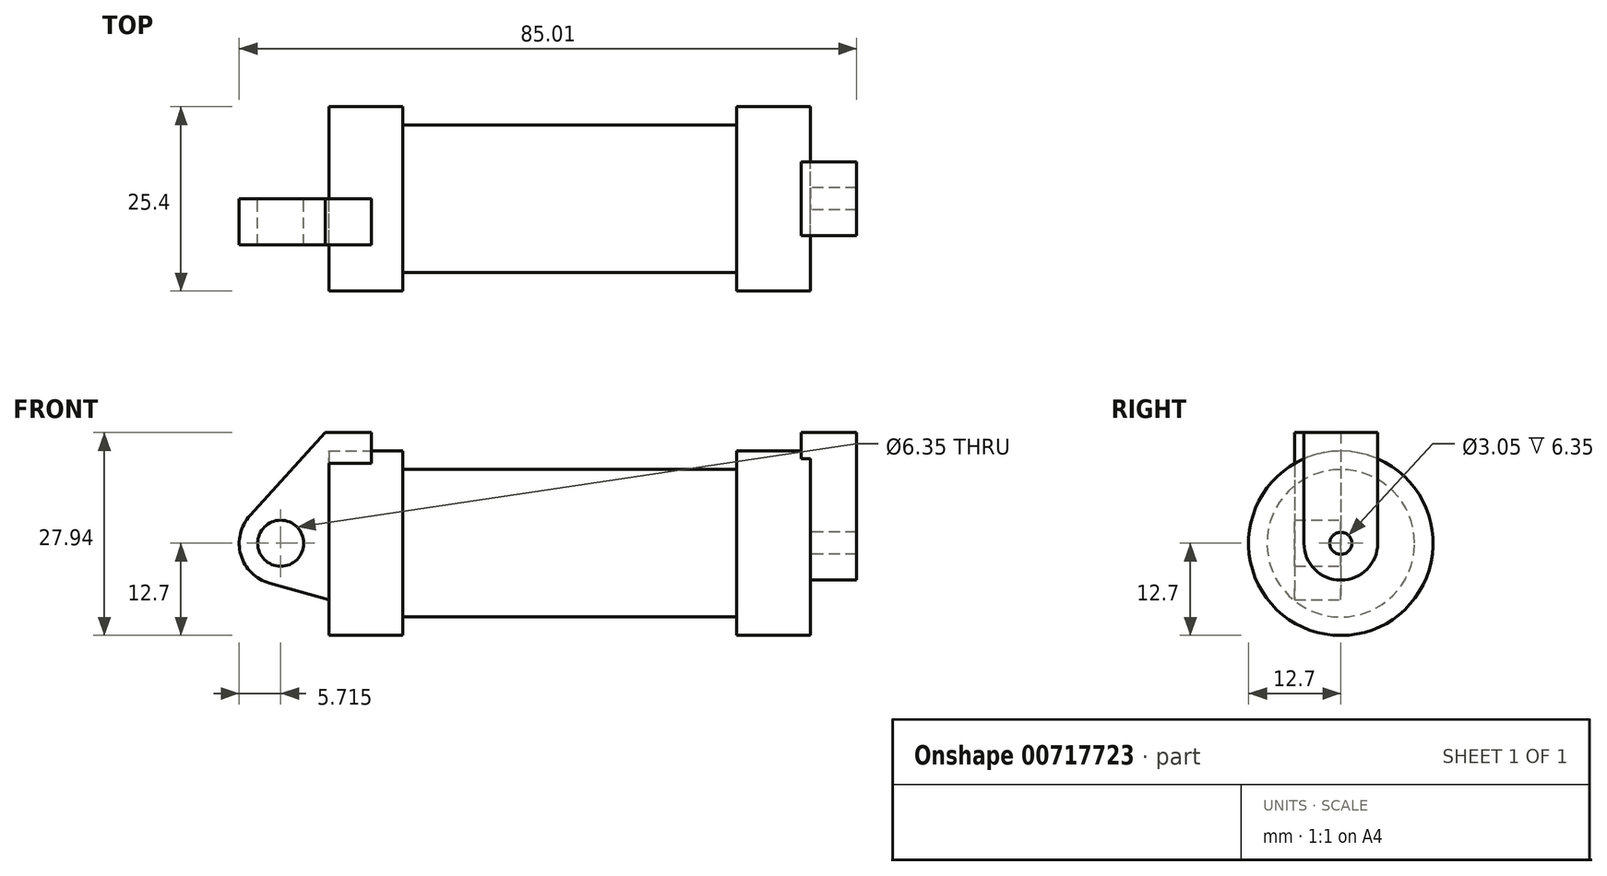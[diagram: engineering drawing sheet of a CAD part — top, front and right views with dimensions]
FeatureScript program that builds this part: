
annotation { "Feature Type Name" : "Feature", "Feature Type Description" : "" }
export const myFeature = defineFeature(function(context is Context, id is Id, definition is map)
    precondition{}
    {
        {
            var Q0;
            Q0=qCreatedBy(makeId("Front.planeOp"),FACE);
            var sketch = newSketch(context, id + "F0", { "sketchPlane" : qUnion([Q0])});
            skLineSegment(sketch, "E0", {"start": v(0, 0) * mm, "end": v(0, 12.7) * mm});
            skLineSegment(sketch, "E1", {"start": v(0, 12.7) * mm, "end": v(10.16, 12.7) * mm});
            skLineSegment(sketch, "E2", {"start": v(10.16, 12.7) * mm, "end": v(10.16, 10.16) * mm});
            skLineSegment(sketch, "E3", {"start": v(10.16, 10.16) * mm, "end": v(56.13, 10.16) * mm});
            skLineSegment(sketch, "E4", {"start": v(56.13, 10.16) * mm, "end": v(56.13, 12.7) * mm});
            skLineSegment(sketch, "E5", {"start": v(56.13, 12.7) * mm, "end": v(66.3, 12.7) * mm});
            skLineSegment(sketch, "E6", {"start": v(66.3, 12.7) * mm, "end": v(66.3, 0) * mm});
            skLineSegment(sketch, "E7", {"start": v(66.3, 0) * mm, "end": v(0, 0) * mm});
            skLineSegment(sketch, "E8", {"start": v(5.84, 15.24) * mm, "end": v(-0.5, 15.24) * mm});
            skLineSegment(sketch, "E9", {"start": v(-0.5, 15.24) * mm, "end": v(-10.88, 3.85) * mm});
            skLineSegment(sketch, "E10", {"start": v(0, 0) * mm, "end": v(-6.65, 0) * mm});
            skCircle(sketch, "E11", {"center": v(-6.65, 0) * mm, "radius": 5.72 * mm});
            skCircle(sketch, "E12", {"center": v(-6.65, 0) * mm, "radius": 3.18 * mm});
            skLineSegment(sketch, "E13", {"start": v(5.84, 15.24) * mm, "end": v(5.84, -9.4) * mm});
            skLineSegment(sketch, "E14", {"start": v(5.84, -9.4) * mm, "end": v(-8.18, -5.5) * mm});
            skSolve(sketch);
        }
        {
            var Q0;
            {var subQ0=sQuery(id+"F0.wireOp",EDGE,"E2");Q0=makeQuery(id+"F0.imprint","IMPRINT",FACE,{"disambiguationData":[TD([[makeQuery(id+"F0.imprint","IMPRINT",EDGE,{"derivedFrom":subQ0}),-1.0]])]});}
            var Q1;
            {var subQ0=sQuery(id+"F0.wireOp",EDGE,"E0");Q1=makeQuery(id+"F0.imprint","IMPRINT",FACE,{"disambiguationData":[TD([[makeQuery(id+"F0.imprint","IMPRINT",EDGE,{"derivedFrom":subQ0}),-1.0]])]});}
            var Q2;
            Q2=sQuery(id+"F0.wireOp",EDGE,"E7");
            revolve(context, id + "F1", {"surfaceOperationType" : NewSurfaceOperationType.NEW, "entities" : qUnion([Q0, Q1]), "axis" : qUnion([Q2]), "revolveType" : RevolveType.FULL});
        }
        {
            var Q0;
            {var subQ1=sQuery(id+"F0.wireOp",EDGE,"E0");Q0=makeQuery(id+"F0.imprint","IMPRINT",FACE,{"disambiguationData":[TD([[makeQuery(id+"F0.imprint","IMPRINT",EDGE,{"derivedFrom":subQ1}),1.0]])]});}
            var Q1;
            {var subQ0=sQuery(id+"F0.wireOp",EDGE,"E14");Q1=makeQuery(id+"F0.imprint","IMPRINT",FACE,{"disambiguationData":[TD([[makeQuery(id+"F0.imprint","IMPRINT",EDGE,{"derivedFrom":subQ0}),-1.0]])]});}
            var Q2;
            {var subQ0=sQuery(id+"F0.wireOp",EDGE,"E0");Q2=makeQuery(id+"F0.imprint","IMPRINT",FACE,{"disambiguationData":[TD([[makeQuery(id+"F0.imprint","IMPRINT",EDGE,{"derivedFrom":subQ0}),-1.0]])]});}
            var Q3;
            {var subQ5=sQuery(id+"F0.wireOp",EDGE,"E12");Q3=makeQuery(id+"F0.imprint","IMPRINT",FACE,{"disambiguationData":[TD([[makeQuery(id+"F0.imprint","IMPRINT",EDGE,{"derivedFrom":subQ5}),-1.0]])]});}
            extrude(context, id + "F2", {"entities" : qUnion([Q0, Q1, Q2, Q3]), "operationType" : NewBodyOperationType.ADD, "depth" : 6.35 * mm, "offsetDistance" : 25.4 * mm});
        }
        {
            var Q0;
            Q0=makeQuery(id+"F1.opRevolve","SWEPT_FACE",FACE,{"disambiguationData":[OSD([sQuery(id+"F0.wireOp",EDGE,"E6")])]});
            var sketch = newSketch(context, id + "F3", { "sketchPlane" : qUnion([Q0])});
            skCircle(sketch, "E15", {"center": v(0, 0) * mm, "radius": 1.52 * mm});
            skCircle(sketch, "E16", {"center": v(0, 0) * mm, "radius": 5.08 * mm});
            skLineSegment(sketch, "E17", {"start": v(-5.08, 0) * mm, "end": v(-5.08, 15.24) * mm});
            skLineSegment(sketch, "E18", {"start": v(5.08, 0) * mm, "end": v(5.08, 15.24) * mm});
            skLineSegment(sketch, "E19", {"start": v(-5.08, 15.24) * mm, "end": v(5.08, 15.24) * mm});
            skSolve(sketch);
        }
        {
            var Q0;
            {var subQ0=sQuery(id+"F3.wireOp",EDGE,"E19");Q0=makeQuery(id+"F3.imprint","IMPRINT",FACE,{"disambiguationData":[TD([[makeQuery(id+"F3.imprint","IMPRINT",EDGE,{"derivedFrom":subQ0}),-1.0]])]});}
            var Q1;
            {var subQ0=sQuery(id+"F3.wireOp",EDGE,"E17");var subQ1=sQuery(id+"F3.wireOp",EDGE,"E16");var subQ2=makeQuery(id+"F3.imprint","INTERSECT",VERTEX,{"derivedFrom":[subQ1,subQ0]});Q1=makeQuery(id+"F3.imprint","IMPRINT",FACE,{"disambiguationData":[TD([[makeQuery(id+"F3.imprint","IMPRINT",EDGE,{"disambiguationData":[TD([[subQ2,1.0]])],"derivedFrom":subQ1}),-1.0]])]});}
            var Q2;
            Q2=makeQuery(id+"F3.imprint","IMPRINT",FACE,{"disambiguationData":[TD([[makeQuery(id+"F3.imprint","IMPRINT",EDGE,{"derivedFrom":sQuery(id+"F3.wireOp",EDGE,"E15")}),-1.0]])]});
            extrude(context, id + "F4", {"entities" : qUnion([Q0, Q1, Q2]), "operationType" : NewBodyOperationType.ADD, "depth" : 6.35 * mm, "offsetDistance" : 25.4 * mm});
        }
        {
            var Q0;
            Q0=makeQuery(id+"F4.opExtrude","CAP_FACE",FACE,{"disambiguationData":[OSD([sQuery(id+"F3.wireOp",EDGE,"E15"),sQuery(id+"F3.wireOp",EDGE,"E16"),sQuery(id+"F3.wireOp",EDGE,"E17"),sQuery(id+"F3.wireOp",EDGE,"E18"),sQuery(id+"F3.wireOp",EDGE,"E19")])],"isStart":false});
            extrude(context, id + "F5", {"entities" : qUnion([Q0]), "operationType" : NewBodyOperationType.ADD, "oppositeDirection" : true, "depth" : 7.62 * mm, "offsetDistance" : 25.4 * mm});
        }
    });
